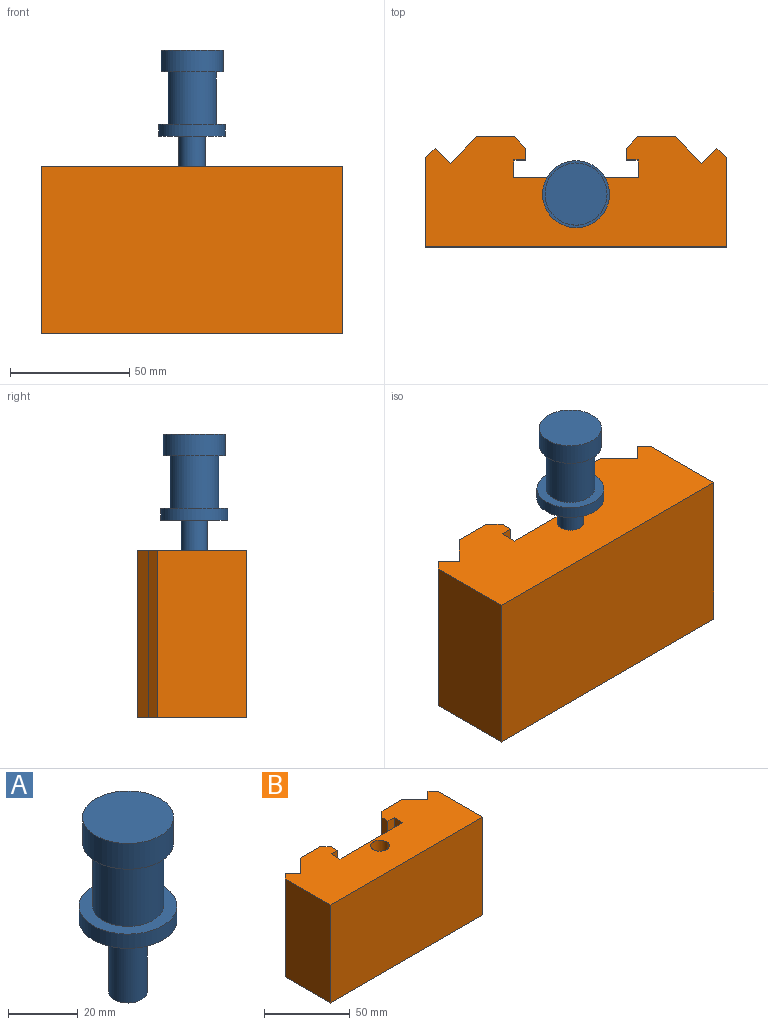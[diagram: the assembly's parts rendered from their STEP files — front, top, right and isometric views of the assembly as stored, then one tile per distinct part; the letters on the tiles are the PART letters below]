
ASSEMBLY  parts=2 mates=1
PART A: 9 faces, bbox 28x28x61.1 mm
  f0: cylinder r=14mm len=28mm, axis (0,0,1), area 439.8mm2, adj f1,f8
  f1: plane 28x28mm, normal (0,0,-1), area 520.7mm2, adj f0,f2
  f2: cylinder r=5.5mm len=25.11mm, axis (0,0,1), area 867.9mm2, adj f1,f3
  f3: plane 11x11mm, normal (0,0,-1), area 95mm2, adj f2
  f4: plane 26x26mm, normal (0,0,1), area 530.9mm2, adj f5
  f5: cylinder r=13mm len=26mm, axis (0,0,1), area 735.1mm2, adj f4,f6
  f6: plane 26x26mm, normal (0,0,-1), area 207.1mm2, adj f5,f7
  f7: cylinder r=10.15mm len=22mm, axis (0,0,1), area 1403.4mm2, adj f6,f8
  f8: plane 28x28mm, normal (0,0,1), area 291.9mm2, adj f0,f7
PART B: 24 faces, bbox 126x46x70 mm
  f0: plane 126x70mm, normal (0,-1,0), area 8820mm2, adj f1,f19,f20,f21
  f1: plane 70x37.31mm, normal (1,0,0), area 2611.5mm2, adj f0,f2,f20,f21
  f2: plane 70x4.03mm, normal (0.71,0.71,0), area 399.3mm2, adj f1,f3,f20,f21
  f3: plane 70x6.31mm, normal (-0.71,0.71,0), area 624.6mm2, adj f2,f4,f20,f21
  f4: plane 70x10.97mm, normal (0.71,0.71,0), area 1085.9mm2, adj f3,f5,f20,f21
  f5: plane 70x16mm, normal (0,1,0), area 1120mm2, adj f4,f6,f20,f21
  f6: plane 70x4.69mm, normal (-0.71,0.71,0), area 464.2mm2, adj f5,f7,f20,f21
  f7: plane 70x4.95mm, normal (-1,0,0), area 346.7mm2, adj f6,f8,f20,f21
  f8: plane 70x5mm, normal (0,-1,0), area 350mm2, adj f7,f9,f20,f21
  f9: plane 70x7.36mm, normal (-1,0,0), area 515.1mm2, adj f8,f10,f20,f21
  f10: plane 70x52mm, normal (0,1,0), area 3640mm2, adj f9,f11,f20,f21
  f11: plane 70x7.36mm, normal (1,0,0), area 515.1mm2, adj f10,f12,f20,f21
  f12: plane 70x5mm, normal (0,-1,0), area 350mm2, adj f11,f13,f20,f21
  f13: plane 70x4.95mm, normal (1,0,0), area 346.7mm2, adj f12,f14,f20,f21
  f14: plane 70x4.69mm, normal (0.71,0.71,0), area 464.2mm2, adj f13,f15,f20,f21
  f15: plane 70x16mm, normal (0,1,0), area 1120mm2, adj f14,f16,f20,f21
  f16: plane 70x10.97mm, normal (-0.71,0.71,0), area 1085.9mm2, adj f15,f17,f20,f21
  f17: plane 70x6.31mm, normal (0.71,0.71,0), area 624.6mm2, adj f16,f18,f20,f21
  f18: plane 70x4.03mm, normal (-0.71,0.71,0), area 399.3mm2, adj f17,f19,f20,f21
  f19: plane 70x37.31mm, normal (-1,0,0), area 2611.5mm2, adj f0,f18,f20,f21
  f20: plane 126x46mm, normal (0,0,1), area 4618.6mm2, adj f0,f1,f2,f3,f4,f5,f6,f7
  f21: plane 126x46mm, normal (0,0,-1), area 4713.7mm2, adj f0,f1,f2,f3,f4,f5,f6,f7
  f22: cylinder r=5.5mm len=40mm, axis (0,0,1), area 1382.3mm2, adj f20,f23
  f23: plane 11x11mm, normal (0,0,1), area 95mm2, adj f22
PLACE A t=(5.55,4.67,47.68)mm
PLACE B t=(5.55,-17.33,-34.84)mm
MATE cylindrical A.f0 <-> B.f22  axis (0,0,1) through (5.55,4.67,22.56)mm
